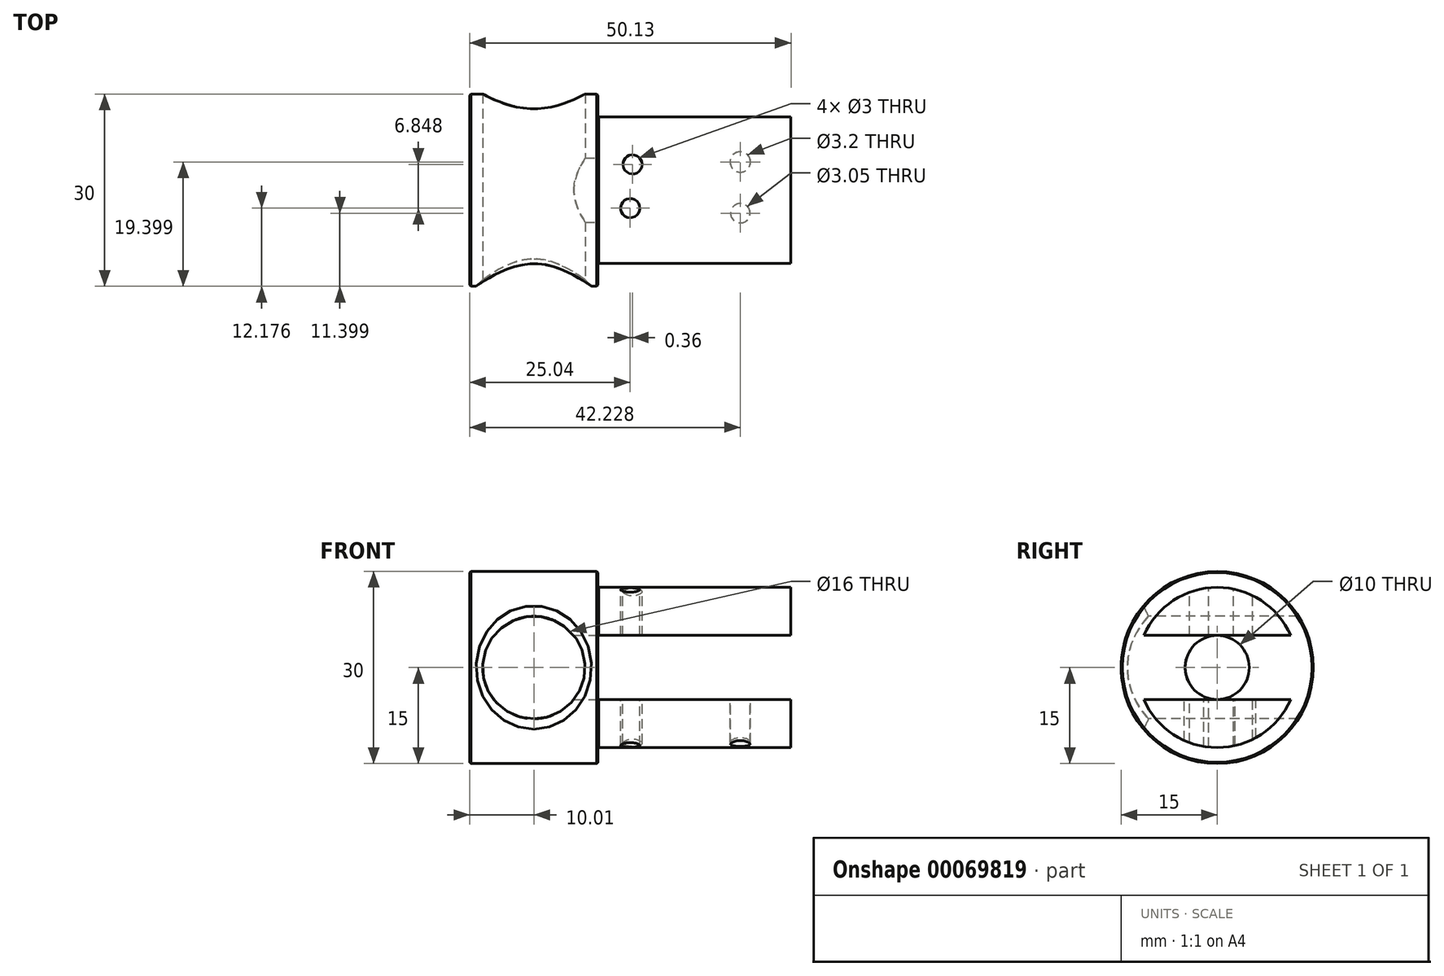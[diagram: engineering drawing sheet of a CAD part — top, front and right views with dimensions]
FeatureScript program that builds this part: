
annotation { "Feature Type Name" : "Feature", "Feature Type Description" : "" }
export const myFeature = defineFeature(function(context is Context, id is Id, definition is map)
    precondition{}
    {
        {
            var Q0;
            Q0=qCreatedBy(makeId("Front.planeOp"),FACE);
            var sketch = newSketch(context, id + "F0", { "sketchPlane" : qUnion([Q0])});
            skLineSegment(sketch, "E0.bottom", {"start": v(-17.8, 15) * mm, "end": v(-37.8, 15) * mm});
            skLineSegment(sketch, "E0.left", {"start": v(-17.8, 15) * mm, "end": v(-17.8, 0) * mm});
            skLineSegment(sketch, "E0.right", {"start": v(-37.8, 15) * mm, "end": v(-37.8, 0) * mm});
            skPoint(sketch, "E0.middle", {"position": v(-27.8, 0) * mm});
            skLineSegment(sketch, "E1.bottom", {"start": v(12.32, 12.5) * mm, "end": v(-17.68, 12.5) * mm});
            skLineSegment(sketch, "E1.left", {"start": v(12.32, 12.5) * mm, "end": v(12.32, 0) * mm});
            skLineSegment(sketch, "E1.right", {"start": v(-17.68, 12.5) * mm, "end": v(-17.68, 0) * mm});
            skPoint(sketch, "E1.middle", {"position": v(-2.68, 0) * mm});
            skLineSegment(sketch, "E2.bottom", {"start": v(12.32, 5) * mm, "end": v(-17.68, 5) * mm});
            skLineSegment(sketch, "E2.left", {"start": v(12.32, 5) * mm, "end": v(12.32, 0) * mm});
            skLineSegment(sketch, "E2.right", {"start": v(-17.68, 5) * mm, "end": v(-17.68, 0) * mm});
            skArc(sketch, "E3", {"start": v(-19.8, 0) * mm, "mid": v(-27.8, 8) * mm, "end": v(-35.8, 0) * mm});
            skCircle(sketch, "E4", {"center": v(61.86, 0) * mm, "radius": 12.5 * mm});
            skLineSegment(sketch, "E5.bottom", {"start": v(50.4, 5) * mm, "end": v(73.31, 5) * mm});
            skLineSegment(sketch, "E5.top", {"start": v(50.4, -5) * mm, "end": v(73.31, -5) * mm});
            skLineSegment(sketch, "E5.left", {"start": v(50.4, 5) * mm, "end": v(50.4, -5) * mm});
            skLineSegment(sketch, "E5.right", {"start": v(73.31, 5) * mm, "end": v(73.31, -5) * mm});
            skLineSegment(sketch, "E6.bottom", {"start": v(73.31, 0) * mm, "end": v(75.4, 0) * mm});
            skLineSegment(sketch, "E6.top", {"start": v(73.31, 0) * mm, "end": v(75.4, 0) * mm});
            skLineSegment(sketch, "E6.left", {"start": v(73.31, 0) * mm, "end": v(73.31, 0) * mm});
            skLineSegment(sketch, "E6.right", {"start": v(75.4, 0) * mm, "end": v(75.4, 0) * mm});
            skPoint(sketch, "E6.middle", {"position": v(74.36, 0) * mm});
            skLineSegment(sketch, "E7", {"start": v(-70.2, 0) * mm, "end": v(34.01, 0) * mm});
            skPoint(sketch, "E8.orphan", {"position": v(-37.8, -15) * mm});
            skPoint(sketch, "E9.orphan", {"position": v(-17.68, -5) * mm});
            skPoint(sketch, "E10.orphan", {"position": v(-17.8, -15) * mm});
            skPoint(sketch, "E1.top.end.orphan", {"position": v(-17.68, -12.5) * mm});
            skPoint(sketch, "E1.top.start.orphan", {"position": v(12.32, -12.5) * mm});
            skPoint(sketch, "E11.orphan", {"position": v(12.32, -5) * mm});
            skSolve(sketch);
        }
        {
            var Q0;
            Q0=makeQuery(id+"F0.imprint","IMPRINT",FACE,{"disambiguationData":[TD([[makeQuery(id+"F0.imprint","IMPRINT",EDGE,{"derivedFrom":sQuery(id+"F0.wireOp",EDGE,"E1.bottom")}),1.0]])]});
            var Q1;
            {var subQ0=sQuery(id+"F0.wireOp",EDGE,"E3");Q1=makeQuery(id+"F0.imprint","IMPRINT",FACE,{"disambiguationData":[TD([[makeQuery(id+"F0.imprint","IMPRINT",EDGE,{"derivedFrom":subQ0}),1.0]])]});}
            var Q2;
            Q2=makeQuery(id+"F0.imprint","IMPRINT",FACE,{"disambiguationData":[TD([[makeQuery(id+"F0.imprint","IMPRINT",EDGE,{"derivedFrom":sQuery(id+"F0.wireOp",EDGE,"E2.bottom")}),1.0]])]});
            var Q3;
            Q3=makeQuery(id+"F0.imprint","IMPRINT",FACE,{"disambiguationData":[TD([[makeQuery(id+"F0.imprint","IMPRINT",EDGE,{"derivedFrom":sQuery(id+"F0.wireOp",EDGE,"E0.bottom")}),1.0]])]});
            var Q4;
            Q4=sQuery(id+"F0.wireOp",EDGE,"E7");
            revolve(context, id + "F1", {"entities" : qUnion([Q0, Q1, Q2, Q3]), "axis" : qUnion([Q4]), "revolveType" : RevolveType.FULL});
        }
        {
            var Q0;
            Q0=makeQuery(id+"F1.opRevolve","SWEPT_FACE",FACE,{"disambiguationData":[OSD([sQuery(id+"F0.wireOp",EDGE,"E1.left"),sQuery(id+"F0.wireOp",EDGE,"E2.left")])]});
            var sketch = newSketch(context, id + "F2", { "sketchPlane" : qUnion([Q0])});
            skLineSegment(sketch, "E12.bottom", {"start": v(23.87, -5) * mm, "end": v(-23.87, -5) * mm});
            skLineSegment(sketch, "E12.top", {"start": v(23.87, 5) * mm, "end": v(-23.87, 5) * mm});
            skLineSegment(sketch, "E12.left", {"start": v(23.87, -5) * mm, "end": v(23.87, 5) * mm});
            skLineSegment(sketch, "E12.right", {"start": v(-23.87, -5) * mm, "end": v(-23.87, 5) * mm});
            skPoint(sketch, "E12.middle", {"position": v(0, 0) * mm});
            skSolve(sketch);
        }
        {
            var Q0;
            {var subQ0=sQuery(id+"F2.wireOp",EDGE,"E12.bottom");var subQ1=makeQuery(id+"F1.opRevolve","SWEPT_EDGE",EDGE,{"disambiguationData":[OSD([sQuery(id+"F0.wireOp",EDGE,"E1.bottom"),sQuery(id+"F0.wireOp",EDGE,"E1.left")])]});var subQ2=makeQuery(id+"F2.imprint","INTERSECT",VERTEX,{"disambiguationData":[OD(0.0)],"derivedFrom":[subQ1,subQ0]});Q0=makeQuery(id+"F2.imprint","IMPRINT",FACE,{"disambiguationData":[TD([[makeQuery(id+"F2.imprint","IMPRINT",EDGE,{"disambiguationData":[TD([[subQ2,-1.0]])],"derivedFrom":subQ0}),-1.0]])]});}
            extrude(context, id + "F3", {"entities" : qUnion([Q0]), "operationType" : NewBodyOperationType.REMOVE, "oppositeDirection" : true, "depth" : 30 * mm});
        }
        {
            var Q0;
            Q0=qCreatedBy(makeId("Front.planeOp"),FACE);
            cPlane(context, id + "F4", {"entities" : qUnion([Q0]), "cplaneType" : CPlaneType.OFFSET, "offset" : 15 * mm, "width" : 150 * mm, "height" : 150 * mm});
        }
        {
            var Q0;
            Q0=qCreatedBy(id+"F4.planeOp",FACE);
            var sketch = newSketch(context, id + "F5", { "sketchPlane" : qUnion([Q0])});
            skLineSegment(sketch, "E13", {"start": v(0, 0) * mm, "end": v(-27.8, 0) * mm});
            skCircle(sketch, "E14", {"center": v(-27.8, 0) * mm, "radius": 8 * mm});
            skSolve(sketch);
        }
        {
            var Q0;
            Q0=makeQuery(id+"F5.imprint","IMPRINT",FACE,{"disambiguationData":[TD([[makeQuery(id+"F5.imprint","IMPRINT",EDGE,{"derivedFrom":sQuery(id+"F5.wireOp",EDGE,"E14")}),1.0]])]});
            extrude(context, id + "F6", {"entities" : qUnion([Q0]), "operationType" : NewBodyOperationType.REMOVE, "oppositeDirection" : true, "depth" : 30 * mm});
        }
        {
            var Q0;
            Q0=makeQuery(id+"F3.boolean.opBoolean","SPLIT",FACE,{"disambiguationData":[TD([makeQuery(id+"F3.opExtrude","SWEPT_FACE",FACE,{"disambiguationData":[OSD([sQuery(id+"F2.wireOp",EDGE,"E12.top")])]})])],"derivedFrom":makeQuery(id+"F1.opRevolve","SWEPT_FACE",FACE,{"disambiguationData":[OSD([sQuery(id+"F0.wireOp",EDGE,"E1.left"),sQuery(id+"F0.wireOp",EDGE,"E2.left")])]})});
            var sketch = newSketch(context, id + "F7", { "sketchPlane" : qUnion([Q0])});
            skCircle(sketch, "E15", {"center": v(0, 0) * mm, "radius": 5 * mm});
            skSolve(sketch);
        }
        {
            var Q0;
            Q0=makeQuery(id+"F7.imprint","IMPRINT",FACE,{"disambiguationData":[TD([[makeQuery(id+"F7.imprint","IMPRINT",EDGE,{"derivedFrom":sQuery(id+"F7.wireOp",EDGE,"E15")}),1.0]])]});
            extrude(context, id + "F8", {"entities" : qUnion([Q0]), "operationType" : NewBodyOperationType.REMOVE, "oppositeDirection" : true, "depth" : 40 * mm});
        }
        {
            var Q0;
            Q0=makeQuery(id+"F1.opRevolve","SWEPT_EDGE",EDGE,{"disambiguationData":[OSD([sQuery(id+"F0.wireOp",EDGE,"E0.bottom"),sQuery(id+"F0.wireOp",EDGE,"E0.left")])]});
            chamfer(context, id + "F9", {"entities" : qUnion([Q0]), "width" : .2 * mm, "tangentPropagation" : true});
        }
        {
            var Q0;
            Q0=makeQuery(id+"F1.opRevolve","SWEPT_EDGE",EDGE,{"disambiguationData":[OSD([sQuery(id+"F0.wireOp",EDGE,"E0.bottom"),sQuery(id+"F0.wireOp",EDGE,"E0.right")])]});
            chamfer(context, id + "F10", {"entities" : qUnion([Q0]), "width" : .2 * mm, "tangentPropagation" : true});
        }
        {
            var Q0;
            Q0=makeQuery(id+"F6.boolean.opBoolean","INTERSECT",EDGE,{"disambiguationData":[OD(0.0)],"derivedFrom":[makeQuery(id+"F1.opRevolve","SWEPT_FACE",FACE,{"disambiguationData":[OSD([sQuery(id+"F0.wireOp",EDGE,"E0.bottom")])]}),makeQuery(id+"F6.opExtrude","SWEPT_FACE",FACE,{"disambiguationData":[OSD([sQuery(id+"F5.wireOp",EDGE,"E14")])]})]});
            chamfer(context, id + "F11", {"entities" : qUnion([Q0]), "width" : 1 * mm, "tangentPropagation" : true});
        }
        {
            var Q0;
            Q0=qCreatedBy(makeId("Top.planeOp"),FACE);
            cPlane(context, id + "F12", {"entities" : qUnion([Q0]), "cplaneType" : CPlaneType.OFFSET, "offset" : 12.5 * mm, "width" : 150 * mm, "height" : 150 * mm});
        }
        {
            var Q0;
            Q0=qCreatedBy(id+"F12.planeOp",FACE);
            var sketch = newSketch(context, id + "F13", { "sketchPlane" : qUnion([Q0])});
            skCircle(sketch, "E16", {"center": v(-12.4, 4.02) * mm, "radius": 1.5 * mm});
            skCircle(sketch, "E17", {"center": v(-12.77, -2.82) * mm, "radius": 1.5 * mm});
            skSolve(sketch);
        }
        {
            var Q0;
            Q0=makeQuery(id+"F13.imprint","IMPRINT",FACE,{"disambiguationData":[TD([[makeQuery(id+"F13.imprint","IMPRINT",EDGE,{"derivedFrom":sQuery(id+"F13.wireOp",EDGE,"E17")}),1.0]])]});
            var Q1;
            Q1=makeQuery(id+"F13.imprint","IMPRINT",FACE,{"disambiguationData":[TD([[makeQuery(id+"F13.imprint","IMPRINT",EDGE,{"derivedFrom":sQuery(id+"F13.wireOp",EDGE,"E16")}),1.0]])]});
            extrude(context, id + "F14", {"entities" : qUnion([Q0, Q1]), "operationType" : NewBodyOperationType.REMOVE, "oppositeDirection" : true, "depth" : 25 * mm});
        }
        {
            var Q0;
            Q0=makeQuery(id+"F3.boolean.opBoolean","COPY",FACE,{"derivedFrom":makeQuery(id+"F3.opExtrude","SWEPT_FACE",FACE,{"disambiguationData":[OSD([sQuery(id+"F2.wireOp",EDGE,"E12.bottom")])]})});
            var sketch = newSketch(context, id + "F15", { "sketchPlane" : qUnion([Q0])});
            skCircle(sketch, "E18", {"center": v(4.42, 4.4) * mm, "radius": 1.6 * mm});
            skCircle(sketch, "E19", {"center": v(4.42, -3.6) * mm, "radius": 1.52 * mm});
            skLineSegment(sketch, "E20", {"start": v(12.32, 3.13) * mm, "end": v(4.42, 4.4) * mm});
            skLineSegment(sketch, "E21", {"start": v(12.32, -4.87) * mm, "end": v(4.42, -3.6) * mm});
            skLineSegment(sketch, "E22", {"start": v(4.42, 4.4) * mm, "end": v(4.42, -3.6) * mm});
            skLineSegment(sketch, "E23", {"start": v(12.32, 3.13) * mm, "end": v(12.32, -4.87) * mm});
            skLineSegment(sketch, "E24", {"start": v(12.32, 3.13) * mm, "end": v(12.32, 11.46) * mm});
            skSolve(sketch);
        }
        {
            var Q0;
            {var subQ0=sQuery(id+"F15.wireOp",EDGE,"E21");var subQ1=sQuery(id+"F15.wireOp",EDGE,"E19");var subQ2=makeQuery(id+"F15.imprint","INTERSECT",VERTEX,{"derivedFrom":[subQ1,subQ0]});Q0=makeQuery(id+"F15.imprint","IMPRINT",FACE,{"disambiguationData":[TD([[makeQuery(id+"F15.imprint","IMPRINT",EDGE,{"disambiguationData":[TD([[subQ2,1.0]])],"derivedFrom":subQ1}),1.0]])]});}
            var Q1;
            {var subQ0=sQuery(id+"F15.wireOp",EDGE,"E21");var subQ1=sQuery(id+"F15.wireOp",EDGE,"E19");var subQ2=makeQuery(id+"F15.imprint","INTERSECT",VERTEX,{"derivedFrom":[subQ1,subQ0]});Q1=makeQuery(id+"F15.imprint","IMPRINT",FACE,{"disambiguationData":[TD([[makeQuery(id+"F15.imprint","IMPRINT",EDGE,{"disambiguationData":[TD([[subQ2,-1.0]])],"derivedFrom":subQ1}),1.0]])]});}
            var Q2;
            {var subQ0=sQuery(id+"F15.wireOp",EDGE,"E20");var subQ1=sQuery(id+"F15.wireOp",EDGE,"E18");var subQ2=makeQuery(id+"F15.imprint","INTERSECT",VERTEX,{"derivedFrom":[subQ1,subQ0]});Q2=makeQuery(id+"F15.imprint","IMPRINT",FACE,{"disambiguationData":[TD([[makeQuery(id+"F15.imprint","IMPRINT",EDGE,{"disambiguationData":[TD([[subQ2,-1.0]])],"derivedFrom":subQ1}),1.0]])]});}
            var Q3;
            {var subQ0=sQuery(id+"F15.wireOp",EDGE,"E20");var subQ1=sQuery(id+"F15.wireOp",EDGE,"E18");var subQ2=makeQuery(id+"F15.imprint","INTERSECT",VERTEX,{"derivedFrom":[subQ1,subQ0]});Q3=makeQuery(id+"F15.imprint","IMPRINT",FACE,{"disambiguationData":[TD([[makeQuery(id+"F15.imprint","IMPRINT",EDGE,{"disambiguationData":[TD([[subQ2,1.0]])],"derivedFrom":subQ1}),1.0]])]});}
            extrude(context, id + "F16", {"entities" : qUnion([Q0, Q1, Q2, Q3]), "operationType" : NewBodyOperationType.REMOVE, "endBound" : BoundingType.THROUGH_ALL, "oppositeDirection" : true, "depth" : 25 * mm});
        }
    });
